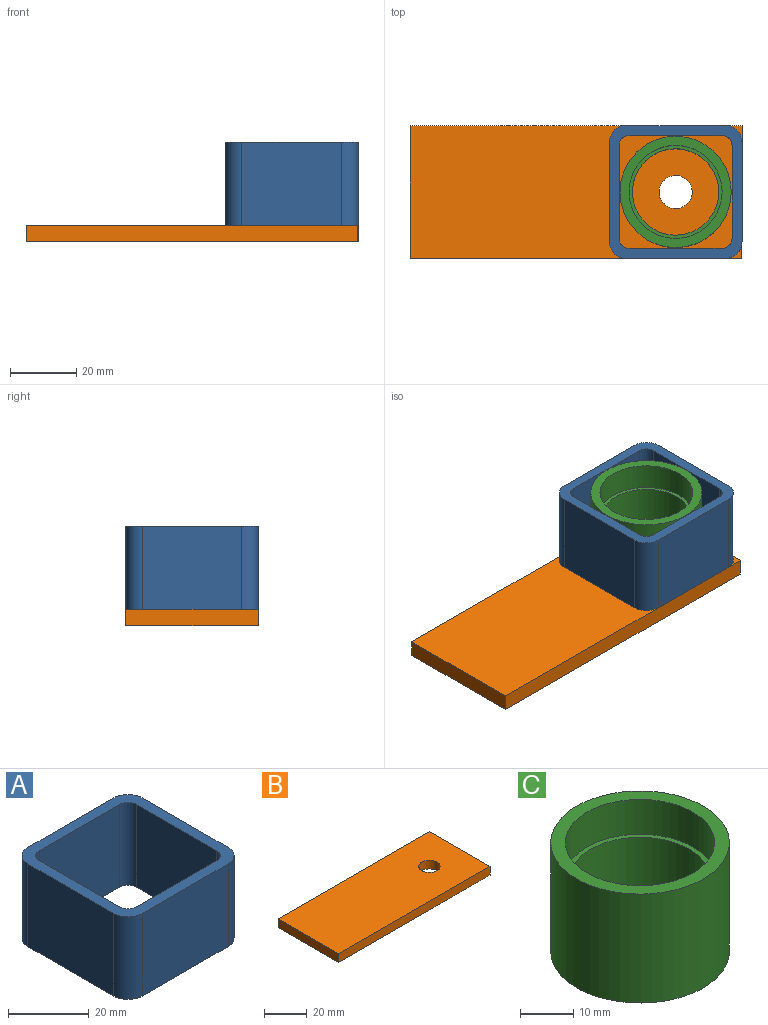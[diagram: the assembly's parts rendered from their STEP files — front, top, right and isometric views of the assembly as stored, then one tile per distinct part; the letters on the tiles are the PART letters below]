
ASSEMBLY  parts=3 mates=2
PART A: 18 faces, bbox 40x40x25 mm
  f0: plane 30x25mm, normal (1,0,0), area 750mm2, adj f1,f15,f16,f17
  f1: cylinder r=5mm len=25mm, axis (0,0,-1), area 196.3mm2, adj f0,f2,f16,f17
  f2: plane 30x25mm, normal (0,1,0), area 750mm2, adj f1,f3,f16,f17
  f3: cylinder r=5mm len=25mm, axis (0,0,-1), area 196.3mm2, adj f2,f4,f16,f17
  f4: plane 30x25mm, normal (-1,0,0), area 750mm2, adj f3,f5,f16,f17
  f5: cylinder r=5mm len=25mm, axis (0,0,-1), area 196.3mm2, adj f4,f6,f16,f17
  f6: plane 30x25mm, normal (0,-1,0), area 750mm2, adj f5,f15,f16,f17
  f7: cylinder r=3mm len=25mm, axis (0,0,-1), area 117.8mm2, adj f8,f14,f16,f17
  f8: plane 28x25mm, normal (-1,0,0), area 700mm2, adj f7,f9,f16,f17
  f9: cylinder r=3mm len=25mm, axis (0,0,-1), area 117.8mm2, adj f8,f10,f16,f17
  f10: plane 28x25mm, normal (0,1,0), area 700mm2, adj f9,f11,f16,f17
  f11: cylinder r=3mm len=25mm, axis (0,0,-1), area 117.8mm2, adj f10,f12,f16,f17
  f12: plane 28x25mm, normal (1,0,0), area 700mm2, adj f11,f13,f16,f17
  f13: cylinder r=3mm len=25mm, axis (0,0,-1), area 117.8mm2, adj f12,f14,f16,f17
  f14: plane 28x25mm, normal (0,-1,0), area 700mm2, adj f7,f13,f16,f17
  f15: cylinder r=5mm len=25mm, axis (0,0,-1), area 196.3mm2, adj f0,f6,f16,f17
  f16: plane 40x40mm, normal (0,0,1), area 430.3mm2, adj f0,f1,f2,f3,f4,f5,f6,f7
  f17: plane 40x40mm, normal (0,0,-1), area 430.3mm2, adj f0,f1,f2,f3,f4,f5,f6,f7
PART B: 7 faces, bbox 100x40x5 mm
  f0: plane 100x5mm, normal (0,-1,0), area 500mm2, adj f1,f4,f5,f6
  f1: plane 40x5mm, normal (1,0,0), area 200mm2, adj f0,f2,f5,f6
  f2: plane 100x5mm, normal (0,1,0), area 500mm2, adj f1,f4,f5,f6
  f3: cylinder r=5mm len=10mm, axis (0,0,-1), area 157.1mm2, adj f5,f6
  f4: plane 40x5mm, normal (-1,0,0), area 200mm2, adj f0,f2,f5,f6
  f5: plane 100x40mm, normal (0,0,1), area 3921.5mm2, adj f0,f1,f2,f3,f4
  f6: plane 100x40mm, normal (0,0,-1), area 3921.5mm2, adj f0,f1,f2,f3,f4
PART C: 6 faces, bbox 33.5x33.5x25 mm
  f0: cylinder r=13mm len=26mm, axis (0,0,-1), area 1388.6mm2, adj f3,f5
  f1: cylinder r=16.75mm len=33.5mm, axis (0,0,-1), area 2631.1mm2, adj f2,f3
  f2: plane 33.5x33.5mm, normal (0,0,1), area 265.7mm2, adj f1,f4
  f3: plane 33.5x33.5mm, normal (0,0,-1), area 350.5mm2, adj f0,f1
  f4: cylinder r=14mm len=28mm, axis (0,0,1), area 703.7mm2, adj f2,f5
  f5: plane 28x28mm, normal (0,0,1), area 84.8mm2, adj f0,f4
PLACE A rot(axis=(1,0,0),180deg) t=(-0.6,-7.64,50.03)mm
PLACE B t=(19.4,-27.64,20.03)mm fixed
PLACE C t=(-0.6,-7.64,25.03)mm
MATE fastened C.f0 <-> B.f3  axis (0,0,-1) through (-0.6,-7.64,25.03)mm
MATE fastened A.f16 <-> B.f3  axis (0,0,-1) through (-0.6,-7.64,25.03)mm
